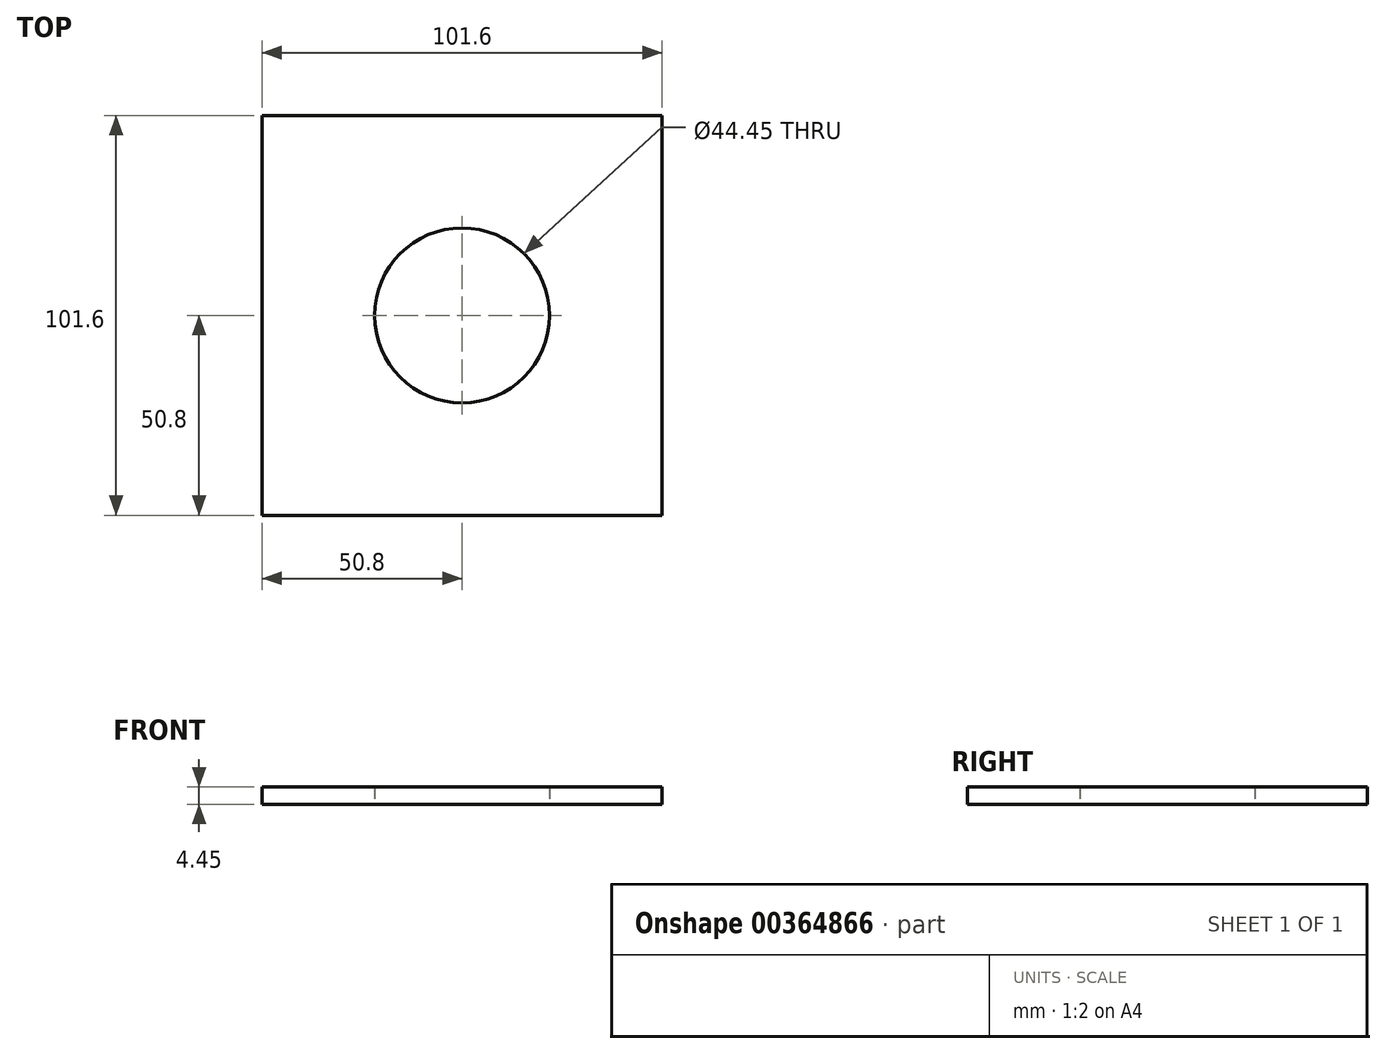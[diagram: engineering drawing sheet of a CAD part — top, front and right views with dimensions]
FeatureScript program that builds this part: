
annotation { "Feature Type Name" : "Feature", "Feature Type Description" : "" }
export const myFeature = defineFeature(function(context is Context, id is Id, definition is map)
    precondition{}
    {
        {
            var Q0;
            Q0=qCreatedBy(makeId("Top.planeOp"),FACE);
            var sketch = newSketch(context, id + "F0", { "sketchPlane" : qUnion([Q0])});
            skLineSegment(sketch, "E0.bottom", {"start": v(-50.8, 50.8) * mm, "end": v(50.8, 50.8) * mm});
            skLineSegment(sketch, "E0.top", {"start": v(-50.8, -50.8) * mm, "end": v(50.8, -50.8) * mm});
            skLineSegment(sketch, "E0.left", {"start": v(-50.8, 50.8) * mm, "end": v(-50.8, -50.8) * mm});
            skLineSegment(sketch, "E0.right", {"start": v(50.8, 50.8) * mm, "end": v(50.8, -50.8) * mm});
            skCircle(sketch, "E1", {"center": v(0, 0) * mm, "radius": 22.23 * mm});
            skSolve(sketch);
        }
        {
            var Q0;
            Q0=makeQuery(id+"F0.imprint","IMPRINT",FACE,{"disambiguationData":[TD([[makeQuery(id+"F0.imprint","IMPRINT",EDGE,{"derivedFrom":sQuery(id+"F0.wireOp",EDGE,"E0.bottom")}),-1.0]])]});
            extrude(context, id + "F1", {"entities" : qUnion([Q0]), "depth" : 4.44 * mm});
        }
    });
